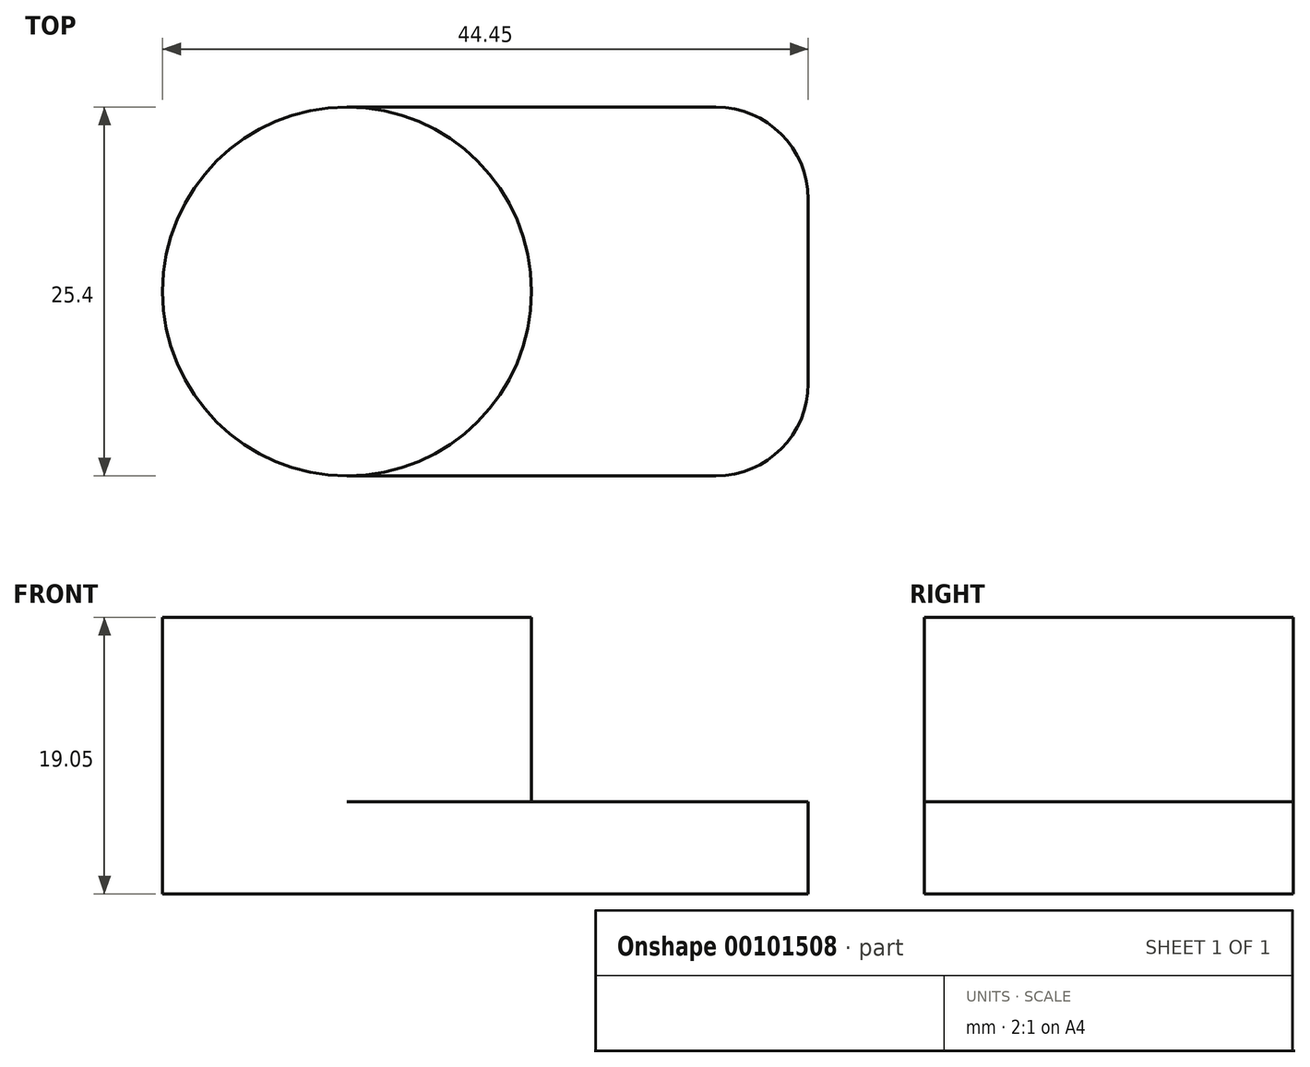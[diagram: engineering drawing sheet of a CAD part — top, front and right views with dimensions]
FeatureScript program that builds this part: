
annotation { "Feature Type Name" : "Feature", "Feature Type Description" : "" }
export const myFeature = defineFeature(function(context is Context, id is Id, definition is map)
    precondition{}
    {
        {
            var Q0;
            Q0=qCreatedBy(makeId("Top.planeOp"),FACE);
            var sketch = newSketch(context, id + "F0", { "sketchPlane" : qUnion([Q0])});
            skCircle(sketch, "E0", {"center": v(12.7, 0) * mm, "radius": 12.7 * mm});
            skSolve(sketch);
        }
        {
            var Q0;
            Q0 = qSketchRegion(id + "F0", true);
            extrude(context, id + "F1", {"entities" : qUnion([Q0]), "depth" : 19.05 * mm});
        }
        {
            var Q0;
            Q0=qCreatedBy(makeId("Top.planeOp"),FACE);
            var sketch = newSketch(context, id + "F2", { "sketchPlane" : qUnion([Q0])});
            skLineSegment(sketch, "E1.bottom", {"start": v(12.7, -12.7) * mm, "end": v(38.1, -12.7) * mm});
            skLineSegment(sketch, "E1.top", {"start": v(12.7, 12.7) * mm, "end": v(38.1, 12.7) * mm});
            skLineSegment(sketch, "E1.left", {"start": v(12.7, -12.7) * mm, "end": v(12.7, 12.7) * mm});
            skLineSegment(sketch, "E1.right", {"start": v(44.45, -6.35) * mm, "end": v(44.45, 6.35) * mm});
            skPoint(sketch, "E2.visualSharp", {"position": v(44.45, -12.7) * mm});
            skArc(sketch, "E2.filletArc", {"start": v(38.1, -12.7) * mm, "mid": v(42.6, -10.84) * mm, "end": v(44.45, -6.35) * mm});
            skPoint(sketch, "E3.visualSharp", {"position": v(44.45, 12.7) * mm});
            skArc(sketch, "E3.filletArc", {"start": v(44.45, 6.35) * mm, "mid": v(42.6, 10.84) * mm, "end": v(38.1, 12.7) * mm});
            skSolve(sketch);
        }
        {
            var Q0;
            Q0 = qSketchRegion(id + "F2", true);
            extrude(context, id + "F3", {"entities" : qUnion([Q0]), "operationType" : NewBodyOperationType.ADD, "depth" : 6.35 * mm});
        }
    });
